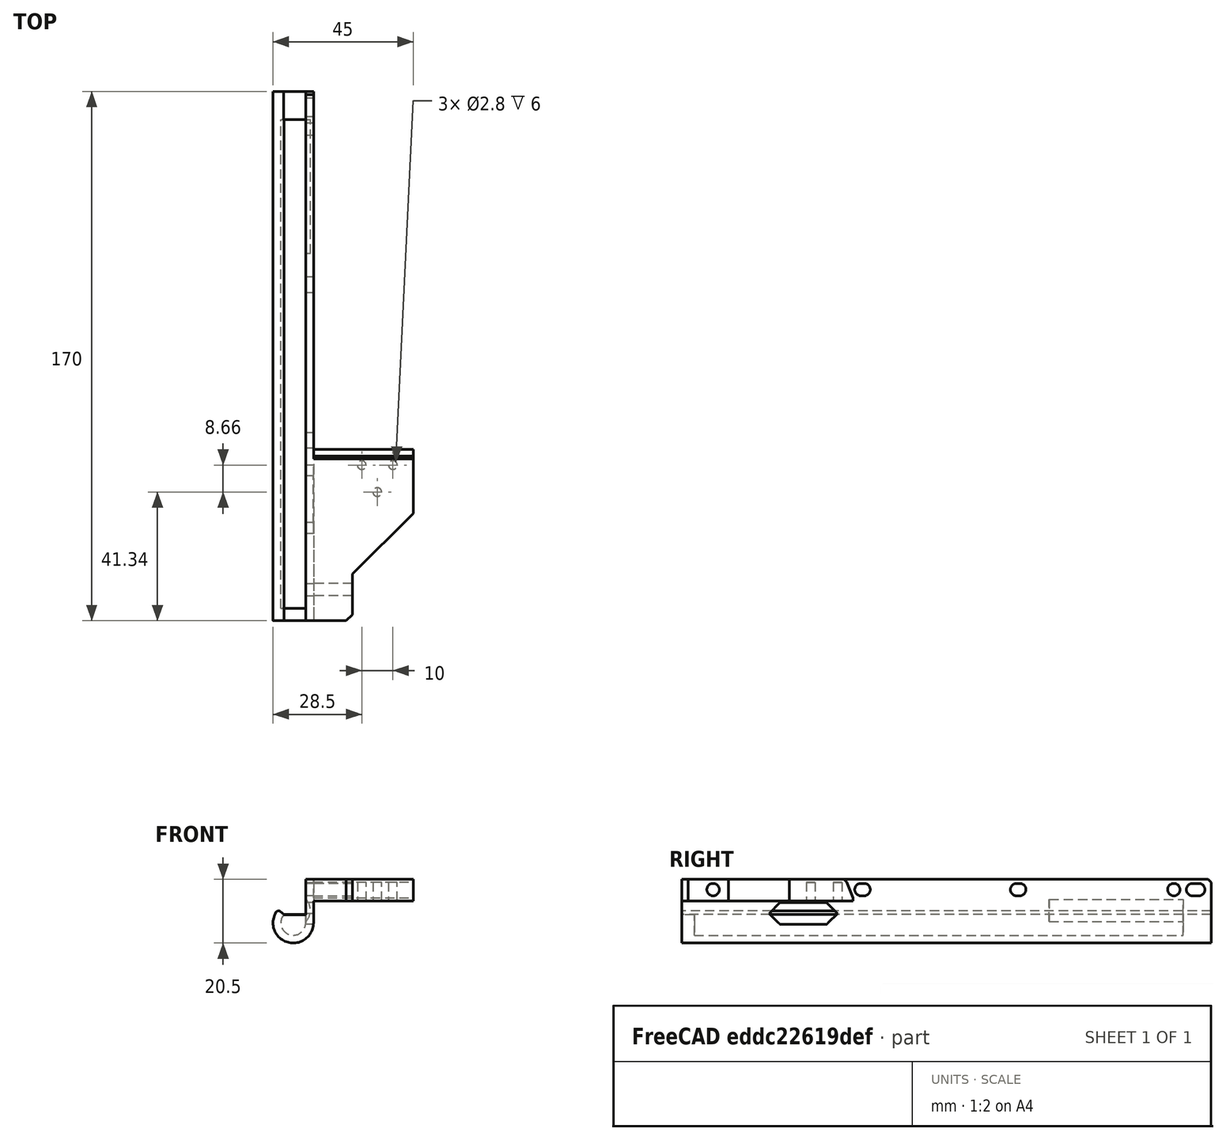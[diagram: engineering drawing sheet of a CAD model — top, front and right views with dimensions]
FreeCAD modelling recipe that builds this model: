
FCSTD DOCUMENT  (FreeCAD 0.19R)
Label: BedChainWire
License: All rights reserved
LicenseURL: http://en.wikipedia.org/wiki/All_rights_reserved
objects: Sketcher::SketchObject×10, PartDesign::Pocket×6, PartDesign::Pad×4, PartDesign::Chamfer×4, PartDesign::Fillet×1, PartDesign::Body×1, Mesh::Feature×1
note: 41 computed .brp shape members not serialized (recipe doc carries the construction recipe); baked Part::Feature solids carry a one-line shape summary decoded from their .brp

FEATURE [Sketcher::SketchObject] Sketch
  FullyConstrained = true
  MapMode = 5
  Placement = pos=(0,0,0) rot=(1,0,0;1.5708rad)
  Support = -> [XZ_Plane]
  sketch-geometry (6):
    g0: LineSegment StartX=0 StartY=0 StartZ=0 EndX=2.5 EndY=0 EndZ=0
    g1: LineSegment StartX=2.5 StartY=0 StartZ=0 EndX=2.5 EndY=-14 EndZ=0
    g2: ArcOfCircle CenterX=-4 CenterY=-14 CenterZ=0 NormalX=0 NormalY=0 NormalZ=1 AngleXU=0 Radius=4 StartAngle=2.41886 EndAngle=6.28319
    g3: ArcOfCircle CenterX=-4 CenterY=-14 CenterZ=0 NormalX=0 NormalY=0 NormalZ=1 AngleXU=0 Radius=6.5 StartAngle=2.41886 EndAngle=6.28319
    g4: LineSegment StartX=0 StartY=0 StartZ=0 EndX=0 EndY=-14 EndZ=0
    g5: LineSegment StartX=-8.875 StartY=-9.70065 StartZ=0 EndX=-7 EndY=-11.3542 EndZ=0
  constraints (16):
    c: Coincident(g-1,g0)
    c: Horizontal(g0)
    c: Coincident(g0,g1)
    c: Vertical(g1)
    c: Coincident(g3,g2)
    c: Tangent(g3,g1) = 1.5708
    c: Coincident(g4,g0)
    c: Vertical(g4)
    c: Tangent(g4,g2) = 1.5708
    c: Coincident(g5,g3)
    c: Coincident(g5,g2)
    c: Diameter(g2) = 8
    c: Perpendicular(g2,g5)
    c: Distance(g5) = 2.5
    c: Distance(g4) = 14
    c: DistanceX(g2) = -7
FEATURE [PartDesign::Pad] Pad
  Direction = (1,1,1)
  Length = 170
  Length2 = 100
  Placement = pos=(0,0,0) rot=(1,0,0;1.5708rad)
  Profile = -> Sketch
  Type = 0
FEATURE [Sketcher::SketchObject] Sketch001  label="mountHoles"
  FullyConstrained = false
  MapMode = 5
  Placement = pos=(2.5,0,0) rot=(0.707107,0,0.707107;3.14159rad)
  Support = -> [Pad]
  sketch-geometry (14):
    g0: Circle CenterX=-3.35 CenterY=12 CenterZ=0 NormalX=0 NormalY=0 NormalZ=1 AngleXU=0 Radius=2
    g1: Circle CenterX=-3.35 CenterY=160 CenterZ=0 NormalX=0 NormalY=0 NormalZ=1 AngleXU=0 Radius=2
    g2: ArcOfCircle CenterX=-3.35 CenterY=6 CenterZ=0 NormalX=0 NormalY=0 NormalZ=1 AngleXU=0 Radius=2 StartAngle=5e-16 EndAngle=3.14159
    g3: ArcOfCircle CenterX=-3.35 CenterY=4 CenterZ=0 NormalX=0 NormalY=0 NormalZ=1 AngleXU=0 Radius=2 StartAngle=3.14159 EndAngle=6.28319
    g4: LineSegment StartX=-5.35 StartY=6 StartZ=0 EndX=-5.35 EndY=4 EndZ=0
    g5: LineSegment StartX=-1.35 StartY=6 StartZ=0 EndX=-1.35 EndY=4 EndZ=0
    g6: ArcOfCircle CenterX=-3.35 CenterY=112.5 CenterZ=0 NormalX=0 NormalY=0 NormalZ=1 AngleXU=0 Radius=2 StartAngle=1.0821e-12 EndAngle=3.14159
    g7: ArcOfCircle CenterX=-3.35 CenterY=111.5 CenterZ=0 NormalX=0 NormalY=0 NormalZ=1 AngleXU=0 Radius=2 StartAngle=3.14159 EndAngle=6.28319
    g8: LineSegment StartX=-5.35 StartY=112.5 StartZ=0 EndX=-5.35 EndY=111.5 EndZ=0
    g9: LineSegment StartX=-1.35 StartY=112.5 StartZ=0 EndX=-1.35 EndY=111.5 EndZ=0
    g10: ArcOfCircle CenterX=-3.35 CenterY=62.5 CenterZ=0 NormalX=0 NormalY=0 NormalZ=1 AngleXU=0 Radius=2 StartAngle=9e-16 EndAngle=3.14159
    g11: ArcOfCircle CenterX=-3.35 CenterY=61.5 CenterZ=0 NormalX=0 NormalY=0 NormalZ=1 AngleXU=0 Radius=2 StartAngle=3.14159 EndAngle=6.28319
    g12: LineSegment StartX=-5.35 StartY=62.5 StartZ=0 EndX=-5.35 EndY=61.5 EndZ=0
    g13: LineSegment StartX=-1.35 StartY=62.5 StartZ=0 EndX=-1.35 EndY=61.5 EndZ=0
  constraints (35):
    c: DistanceY(g0) = 12
    c: DistanceX(g0) = -3.35
    c: DistanceX(g1) = -3.35
    c: Diameter(g1) = 4
    c: Equal(g1,g0)
    c: Tangent(g2,g5) = 1.5708
    c: Tangent(g2,g4) = -1.5708
    c: Tangent(g4,g3) = -1.5708
    c: Tangent(g5,g3) = 1.5708
    c: Vertical(g4)
    c: Equal(g2,g3)
    c: Distance(g2,g2) = 4
    c: Distance(g2,g3) = 2
    c: DistanceY(g2) = 6
    c: DistanceX(g2) = -3.35
    c: Tangent(g6,g9) = 1.5708
    c: Tangent(g6,g8) = -1.5708
    c: Tangent(g8,g7) = -1.5708
    c: Tangent(g9,g7) = 1.5708
    c: Vertical(g8)
    c: Equal(g6,g7)
    c: Distance(g6,g6) = 4
    c: Distance(g7,g6) = 1
    c: DistanceX(g6) = -3.35
    c: Tangent(g10,g13) = 1.5708
    c: Tangent(g10,g12) = -1.5708
    c: Tangent(g12,g11) = -1.5708
    c: Tangent(g13,g11) = 1.5708
    c: Vertical(g12)
    c: Equal(g10,g11)
    c: Distance(g10,g11) = 1
    c: Distance(g10,g10) = 4
    c: Distance(g0,g10) = 50.5
    c: DistanceX(g10) = -3.35
    c: Distance(g6,g10) = 50
FEATURE [PartDesign::Pocket] Pocket
  BaseFeature = -> Pad
  Length = 5
  Length2 = 100
  Placement = pos=(0,0,0) rot=(1,0,0;1.5708rad)
  Profile = -> Sketch001
  Type = 0
FEATURE [Sketcher::SketchObject] Sketch003  label="chainpad"
  FullyConstrained = true
  MapMode = 5
  Placement = pos=(2.5,0,0) rot=(0.707107,0,0.707107;3.14159rad)
  Support = -> [Pocket]
  sketch-geometry (4):
    g0: LineSegment StartX=-7 StartY=170 StartZ=0 EndX=0 EndY=170 EndZ=0
    g1: LineSegment StartX=0 StartY=170 StartZ=0 EndX=0 EndY=115 EndZ=0
    g2: LineSegment StartX=0 StartY=115 StartZ=0 EndX=-7 EndY=115 EndZ=0
    g3: LineSegment StartX=-7 StartY=115 StartZ=0 EndX=-7 EndY=170 EndZ=0
  constraints (12):
    c: Coincident(g0,g1)
    c: Coincident(g1,g2)
    c: Coincident(g2,g3)
    c: Coincident(g3,g0)
    c: Horizontal(g0)
    c: Horizontal(g2)
    c: Vertical(g1)
    c: Vertical(g3)
    c: Distance(g0) = 7
    c: PointOnObject(g0,g-2)
    c: DistanceY(g0) = 170
    c: Distance(g3) = 55
FEATURE [PartDesign::Pad] Pad001
  BaseFeature = -> Pocket
  Direction = (1,1,1)
  Length = 32
  Length2 = 100
  Placement = pos=(0,0,0) rot=(1,0,0;1.5708rad)
  Profile = -> Sketch003
  Type = 0
FEATURE [Sketcher::SketchObject] Sketch004  label="wireExit"
  FullyConstrained = true
  MapMode = 5
  Placement = pos=(2.5,0,0) rot=(0.707107,0,0.707107;3.14159rad)
  Support = -> [Pad001]
  sketch-geometry (6):
    g0: LineSegment StartX=-11 StartY=142 StartZ=0 EndX=-7.5 EndY=138.5 EndZ=0
    g1: LineSegment StartX=-7.5 StartY=138.5 StartZ=0 EndX=-7.5 EndY=123.5 EndZ=0
    g2: LineSegment StartX=-7.5 StartY=123.5 StartZ=0 EndX=-11 EndY=120 EndZ=0
    g3: LineSegment StartX=-11 StartY=120 StartZ=0 EndX=-14.5 EndY=123.5 EndZ=0
    g4: LineSegment StartX=-14.5 StartY=123.5 StartZ=0 EndX=-14.5 EndY=138.5 EndZ=0
    g5: LineSegment StartX=-14.5 StartY=138.5 StartZ=0 EndX=-11 EndY=142 EndZ=0
  constraints (18):
    c: Coincident(g0,g1)
    c: Vertical(g1)
    c: Coincident(g1,g2)
    c: Coincident(g2,g3)
    c: Coincident(g3,g4)
    c: Vertical(g4)
    c: Coincident(g4,g5)
    c: Coincident(g5,g0)
    c: Equal(g5,g0)
    c: Equal(g0,g3)
    c: Equal(g3,g2)
    c: Angle(g0) = -0.785398
    c: Angle(g2) = -2.35619
    c: Distance(g0,g4) = 7
    c: Equal(g1,g4)
    c: Distance(g4) = 15
    c: DistanceX(g1) = -7.5
    c: DistanceY(g2) = 120
FEATURE [PartDesign::Pocket] Pocket001
  BaseFeature = -> Pad001
  Length = 5
  Length2 = 100
  Placement = pos=(0,0,0) rot=(1,0,0;1.5708rad)
  Profile = -> Sketch004
  Type = 0
FEATURE [Sketcher::SketchObject] Sketch005  label="chainattachholes"
  FullyConstrained = false
  MapMode = 5
  Placement = pos=(-1.6e-15,1.6e-15,-7) rot=(1,0,0;3.14159rad)
  Support = -> [Pocket001]
  sketch-geometry (7):
    g0: Circle CenterX=28 CenterY=120 CenterZ=0 NormalX=0 NormalY=0 NormalZ=1 AngleXU=0 Radius=1.4
    g1: Circle CenterX=18 CenterY=120 CenterZ=0 NormalX=0 NormalY=0 NormalZ=1 AngleXU=0 Radius=1.4
    g2: Circle CenterX=23 CenterY=128.66 CenterZ=0 NormalX=0 NormalY=0 NormalZ=1 AngleXU=0 Radius=1.4
    g3: LineSegment StartX=18 StartY=120 StartZ=0 EndX=28 EndY=120 EndZ=0
    g4: LineSegment StartX=28 StartY=120 StartZ=0 EndX=23 EndY=128.66 EndZ=0
    g5: LineSegment StartX=23 StartY=128.66 StartZ=0 EndX=18 EndY=120 EndZ=0
    g6: LineSegment StartX=34.5 StartY=128.862 StartZ=0 EndX=34.5 EndY=122.881 EndZ=0
  constraints (17):
    c: Coincident(g3,g1)
    c: Coincident(g3,g0)
    c: Coincident(g3,g4)
    c: Coincident(g4,g2)
    c: Coincident(g4,g5)
    c: Coincident(g5,g3)
    c: Equal(g4,g3)
    c: Equal(g3,g5)
    c: Diameter(g0) = 2.8
    c: Equal(g0,g2)
    c: Equal(g0,g1)
    c: Distance(g3) = 10
    c: Horizontal(g3)
    c: Distance(g0,g6) = 6.5
    c: Vertical(g6)
    c: DistanceX(g0) = 28
    c: DistanceY(g0) = 120
FEATURE [Sketcher::SketchObject] Sketch006  label="cableclearance"
  FullyConstrained = true
  MapMode = 5
  Placement = pos=(0,0,0) rot=(-1,0,0;1.5708rad)
  sketch-geometry (2):
    g0: ArcOfCircle CenterX=-3.5 CenterY=10 CenterZ=0 NormalX=0 NormalY=0 NormalZ=1 AngleXU=0 Radius=5 StartAngle=4.71239 EndAngle=7.85398
    g1: LineSegment StartX=-3.5 StartY=15 StartZ=0 EndX=-3.5 EndY=5 EndZ=0
  constraints (7):
    c: Diameter(g0) = 10
    c: DistanceY(g0) = 10
    c: DistanceX(g0) = -3.5
    c: Coincident(g1,g0)
    c: Coincident(g1,g0)
    c: Vertical(g1)
    c: PointOnObject(g0,g1)
FEATURE [Sketcher::SketchObject] Sketch007  label="hole"
  FullyConstrained = true
  MapMode = 5
  Placement = pos=(0,0,0) rot=(0.707107,0,-0.707107;3.14159rad)
  sketch-geometry (1):
    g0: Circle CenterX=3.35 CenterY=160 CenterZ=0 NormalX=0 NormalY=0 NormalZ=1 AngleXU=0 Radius=2
  constraints (3):
    c: Diameter(g0) = 4
    c: DistanceX(g0) = 3.35
    c: DistanceY(g0) = 160
FEATURE [Sketcher::SketchObject] Sketch008  label="frontreleif"
  FullyConstrained = false
  MapMode = 5
  Placement = pos=(0,0,1e-15) rot=(0,0,1;3.14159rad)
  sketch-geometry (4):
    g0: LineSegment StartX=-15 StartY=171.39 StartZ=0 EndX=-15 EndY=155 EndZ=0
    g1: LineSegment StartX=-15 StartY=155 StartZ=0 EndX=-43.5876 EndY=126.412 EndZ=0
    g2: LineSegment StartX=-43.5876 StartY=126.412 StartZ=0 EndX=-43.5876 EndY=179.575 EndZ=0
    g3: LineSegment StartX=-43.5876 StartY=179.575 StartZ=0 EndX=-15 EndY=171.39 EndZ=0
  constraints (9):
    c: Vertical(g0)
    c: Coincident(g0,g1)
    c: Coincident(g1,g2)
    c: Vertical(g2)
    c: Coincident(g2,g3)
    c: Coincident(g3,g0)
    c: DistanceX(g0) = -15
    c: DistanceY(g0) = 155
    c: Angle(g1) = -2.35619
FEATURE [Sketcher::SketchObject] Sketch009  label="endcap"
  FullyConstrained = false
  MapMode = 5
  Placement = pos=(0,0,0) rot=(-1,0,0;1.5708rad)
  sketch-geometry (7):
    g0: LineSegment StartX=-8.98889 StartY=11.3212 StartZ=0 EndX=0 EndY=11.3212 EndZ=0
    g1: LineSegment StartX=1.76076 StartY=16.1529 StartZ=0 EndX=-3.18457 EndY=19.1762 EndZ=0
    g2: LineSegment StartX=-3.18457 StartY=19.1762 StartZ=0 EndX=-9.01349 EndY=16.4741 EndZ=0
    g3: LineSegment StartX=-9.01349 StartY=16.4741 StartZ=0 EndX=-8.98889 EndY=11.3212 EndZ=0
    g4: LineSegment StartX=0 StartY=11.3212 StartZ=0 EndX=0 EndY=5.37564 EndZ=0
    g5: LineSegment StartX=0 StartY=5.37564 StartZ=0 EndX=1.76076 EndY=5.37564 EndZ=0
    g6: LineSegment StartX=1.76076 StartY=5.37564 StartZ=0 EndX=1.76076 EndY=16.1529 EndZ=0
  constraints (12):
    c: Horizontal(g0)
    c: Coincident(g1,g2)
    c: Coincident(g2,g3)
    c: Coincident(g3,g0)
    c: PointOnObject(g0,g-2)
    c: Coincident(g0,g4)
    c: PointOnObject(g4,g-2)
    c: Coincident(g4,g5)
    c: Horizontal(g5)
    c: Coincident(g5,g6)
    c: Coincident(g6,g1)
    c: Vertical(g6)
FEATURE [Sketcher::SketchObject] Sketch010  label="frontcap"
  FullyConstrained = false
  MapMode = 5
  Placement = pos=(0,-170,2.26e-13) rot=(1,0,0;1.5708rad)
  sketch-geometry (8):
    g0: LineSegment StartX=1.60772 StartY=-11.3921 StartZ=0 EndX=-8.31304 EndY=-11.3921 EndZ=0
    g1: LineSegment StartX=-8.31304 StartY=-11.3921 StartZ=0 EndX=-9.51489 EndY=-14.3198 EndZ=0
    g2: LineSegment StartX=-9.51489 StartY=-14.3198 StartZ=0 EndX=-8.85866 EndY=-17.0991 EndZ=0
    g3: LineSegment StartX=-8.85866 StartY=-17.0991 StartZ=0 EndX=-6.11791 EndY=-19.2222 EndZ=0
    g4: LineSegment StartX=-6.11791 StartY=-19.2222 StartZ=0 EndX=-3.18414 EndY=-19.2222 EndZ=0
    g5: LineSegment StartX=-3.18414 StartY=-19.2222 StartZ=0 EndX=0.714678 EndY=-18.1028 EndZ=0
    g6: LineSegment StartX=0.714678 StartY=-18.1028 StartZ=0 EndX=1.60772 EndY=-15.7094 EndZ=0
    g7: LineSegment StartX=1.60772 StartY=-15.7094 StartZ=0 EndX=1.60772 EndY=-11.3921 EndZ=0
  constraints (11):
    c: Horizontal(g0)
    c: Coincident(g0,g1)
    c: Coincident(g1,g2)
    c: Coincident(g2,g3)
    c: Coincident(g3,g4)
    c: Horizontal(g4)
    c: Coincident(g4,g5)
    c: Coincident(g5,g6)
    c: Coincident(g6,g7)
    c: Coincident(g7,g0)
    c: Vertical(g7)
FEATURE [PartDesign::Pocket] Pocket002
  BaseFeature = -> Pocket001
  Length = 6
  Length2 = 100
  Placement = pos=(0,0,0) rot=(1,0,0;1.5708rad)
  Profile = -> Sketch005
  Type = 0
FEATURE [PartDesign::Pocket] Pocket003
  BaseFeature = -> Pocket002
  Length = 52
  Length2 = 100
  Placement = pos=(0,0,0) rot=(1,0,0;1.5708rad)
  Profile = -> Sketch006
  Type = 0
FEATURE [PartDesign::Pocket] Pocket004
  BaseFeature = -> Pocket003
  Length = 5
  Length2 = 100
  Placement = pos=(0,0,0) rot=(1,0,0;1.5708rad)
  Profile = -> Sketch007
  Type = 1
FEATURE [PartDesign::Pocket] Pocket005
  BaseFeature = -> Pocket004
  Length = 5
  Length2 = 100
  Placement = pos=(0,0,0) rot=(1,0,0;1.5708rad)
  Profile = -> Sketch008
  Type = 1
FEATURE [PartDesign::Pad] Pad002
  BaseFeature = -> Pocket005
  Direction = (1,1,1)
  Length = 9
  Length2 = 100
  Placement = pos=(0,0,0) rot=(1,0,0;1.5708rad)
  Profile = -> Sketch009
  Reversed = true
  Type = 0
FEATURE [PartDesign::Pad] Pad003
  BaseFeature = -> Pad002
  Direction = (1,1,1)
  Length = 4
  Length2 = 100
  Placement = pos=(0,0,0) rot=(1,0,0;1.5708rad)
  Profile = -> Sketch010
  Reversed = true
  Type = 0
FEATURE [PartDesign::Fillet] Fillet
  Base = -> Pad003 [Edge130]
  BaseFeature = -> Pad003
  Placement = pos=(0,0,0) rot=(1,0,0;1.5708rad)
  Radius = 1
  SupportTransform = false
FEATURE [PartDesign::Chamfer] Chamfer
  Angle = 45
  Base = -> Fillet [Edge153]
  BaseFeature = -> Fillet
  ChamferType = 0
  FlipDirection = false
  Placement = pos=(0,0,0) rot=(1,0,0;1.5708rad)
  Size = 2
  Size2 = 1
  SupportTransform = false
FEATURE [PartDesign::Chamfer] Chamfer001
  Angle = 45
  Base = -> Chamfer [Edge43]
  BaseFeature = -> Chamfer
  ChamferType = 0
  FlipDirection = false
  Placement = pos=(0,0,0) rot=(1,0,0;1.5708rad)
  Size = 3
  Size2 = 1
  SupportTransform = false
FEATURE [PartDesign::Chamfer] Chamfer002
  Angle = 45
  Base = -> Chamfer001 [Edge28]
  BaseFeature = -> Chamfer001
  ChamferType = 0
  FlipDirection = false
  Placement = pos=(0,0,0) rot=(1,0,0;1.5708rad)
  Size = 3
  Size2 = 1
  SupportTransform = false
FEATURE [PartDesign::Chamfer] Chamfer003
  Angle = 45
  Base = -> Chamfer002 [Edge62]
  BaseFeature = -> Chamfer002
  ChamferType = 0
  FlipDirection = false
  Placement = pos=(0,0,0) rot=(1,0,0;1.5708rad)
  Size = 1
  Size2 = 1
  SupportTransform = false
FEATURE [PartDesign::Body] Body
  Group = -> [Sketch,Pad,Sketch001,Pocket,Sketch003,Pad001,Sketch004,Pocket001,Sketch005,Sketch006,Sketch007,Sketch008,Sketch009,Sketch010,Pocket002,Pocket003,Pocket004,Pocket005,Pad002,Pad003,Fillet,Chamfer,Chamfer001,Chamfer002,Chamfer003]
  Origin = -> Origin
  Tip = -> Chamfer003
FEATURE [Mesh::Feature] Mesh  label="Chamfer003 (Meshed)"
